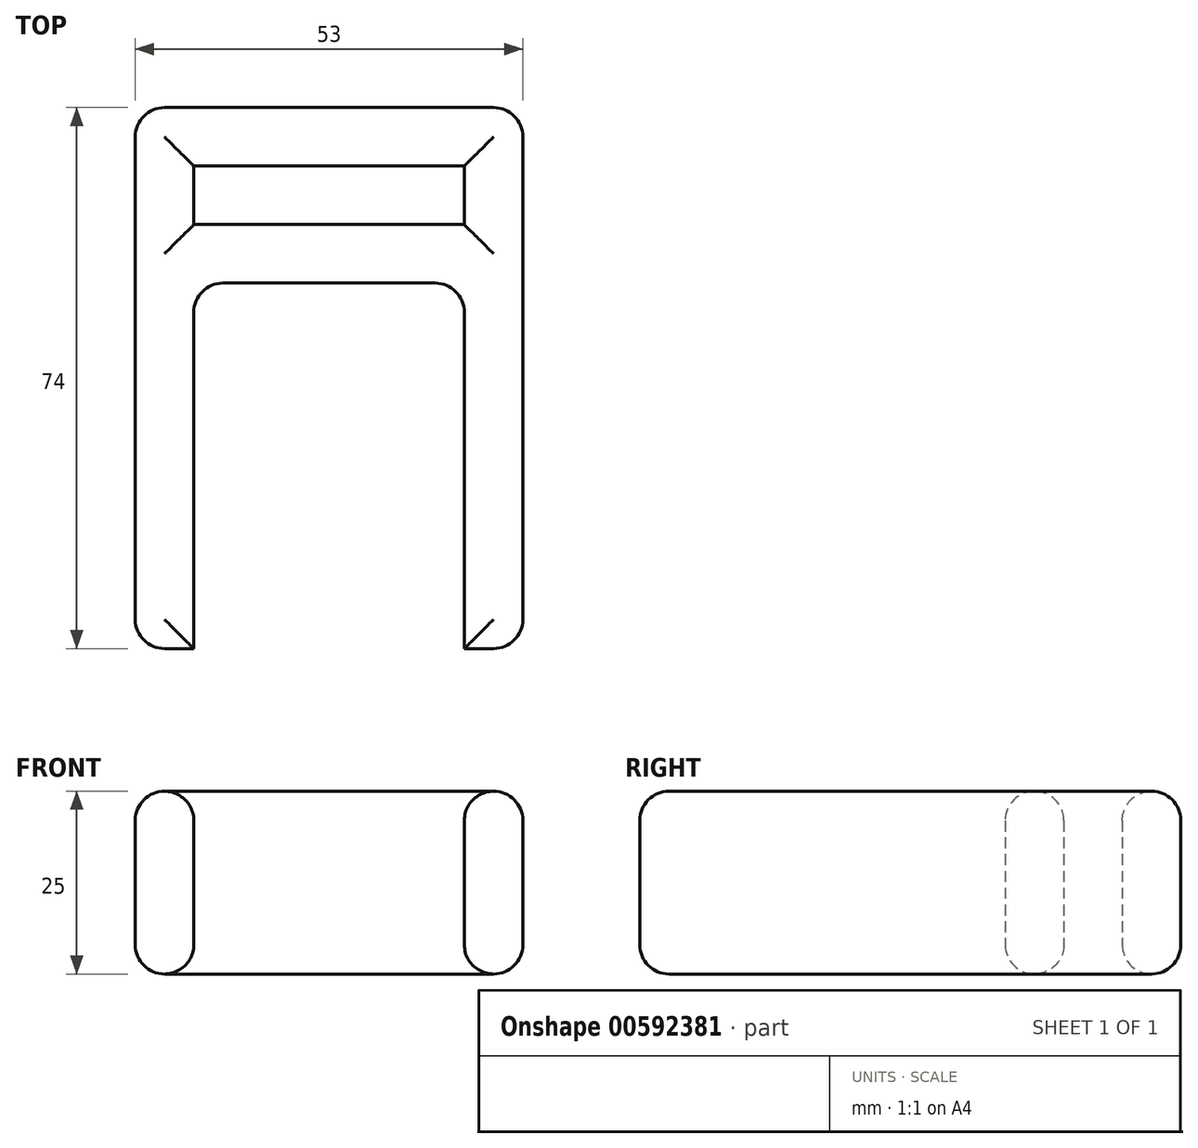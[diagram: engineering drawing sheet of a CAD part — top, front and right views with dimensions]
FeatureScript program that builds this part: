
annotation { "Feature Type Name" : "Feature", "Feature Type Description" : "" }
export const myFeature = defineFeature(function(context is Context, id is Id, definition is map)
    precondition{}
    {
        {
            var Q0;
            Q0=qCreatedBy(makeId("Top.planeOp"),FACE);
            var sketch = newSketch(context, id + "F0", { "sketchPlane" : qUnion([Q0])});
            skLineSegment(sketch, "E0.bottom", {"start": v(18.5, -25) * mm, "end": v(-18.5, -25) * mm});
            skLineSegment(sketch, "E0.top", {"start": v(18.5, 25) * mm, "end": v(-18.5, 25) * mm});
            skLineSegment(sketch, "E0.left", {"start": v(18.5, -25) * mm, "end": v(18.5, 25) * mm});
            skLineSegment(sketch, "E0.right", {"start": v(-18.5, -25) * mm, "end": v(-18.5, 25) * mm});
            skPoint(sketch, "E0.middle", {"position": v(0, 0) * mm});
            skLineSegment(sketch, "E1", {"start": v(-18.5, -25) * mm, "end": v(-26.5, -25) * mm});
            skLineSegment(sketch, "E2", {"start": v(18.5, -25) * mm, "end": v(26.5, -25) * mm});
            skLineSegment(sketch, "E3.bottom", {"start": v(-26.5, -25) * mm, "end": v(26.5, -25) * mm});
            skLineSegment(sketch, "E3.top", {"start": v(-26.5, 33) * mm, "end": v(26.5, 33) * mm});
            skLineSegment(sketch, "E3.left", {"start": v(-26.5, -25) * mm, "end": v(-26.5, 33) * mm});
            skLineSegment(sketch, "E3.right", {"start": v(26.5, -25) * mm, "end": v(26.5, 33) * mm});
            skLineSegment(sketch, "E4.top", {"start": v(-26.5, 49) * mm, "end": v(26.5, 49) * mm});
            skLineSegment(sketch, "E4.left", {"start": v(-26.5, 33) * mm, "end": v(-26.5, 49) * mm});
            skLineSegment(sketch, "E4.right", {"start": v(26.5, 33) * mm, "end": v(26.5, 49) * mm});
            skLineSegment(sketch, "E5.bottom", {"start": v(-18.5, 33) * mm, "end": v(18.5, 33) * mm});
            skLineSegment(sketch, "E5.top", {"start": v(-18.5, 41) * mm, "end": v(18.5, 41) * mm});
            skLineSegment(sketch, "E5.left", {"start": v(-18.5, 33) * mm, "end": v(-18.5, 41) * mm});
            skLineSegment(sketch, "E5.right", {"start": v(18.5, 33) * mm, "end": v(18.5, 41) * mm});
            skSolve(sketch);
        }
        {
            var Q0;
            Q0=makeQuery(id+"F0.imprint","IMPRINT",FACE,{"disambiguationData":[TD([[makeQuery(id+"F0.imprint","IMPRINT",EDGE,{"derivedFrom":sQuery(id+"F0.wireOp",EDGE,"E0.top")}),-1.0]])]});
            var Q1;
            Q1=makeQuery(id+"F0.imprint","IMPRINT",FACE,{"disambiguationData":[TD([[makeQuery(id+"F0.imprint","IMPRINT",EDGE,{"derivedFrom":sQuery(id+"F0.wireOp",EDGE,"E4.top")}),-1.0]])]});
            extrude(context, id + "F1", {"entities" : qUnion([Q0, Q1]), "depth" : 25 * mm, "offsetDistance" : 25 * mm});
        }
        {
            var Q0;
            Q0=makeQuery(id+"F1.opExtrude","SWEPT_EDGE",EDGE,{"disambiguationData":[OSD([sQuery(id+"F0.wireOp",EDGE,"E4.top"),sQuery(id+"F0.wireOp",EDGE,"E4.left")])]});
            var Q1;
            Q1=makeQuery(id+"F1.opExtrude","SWEPT_EDGE",EDGE,{"disambiguationData":[OSD([sQuery(id+"F0.wireOp",EDGE,"E4.top"),sQuery(id+"F0.wireOp",EDGE,"E4.right")])]});
            var Q2;
            Q2=makeQuery(id+"F1.opExtrude","SWEPT_EDGE",EDGE,{"disambiguationData":[OSD([sQuery(id+"F0.wireOp",EDGE,"E0.right"),sQuery(id+"F0.wireOp",EDGE,"E3.bottom")])]});
            var Q3;
            Q3=makeQuery(id+"F1.opExtrude","SWEPT_EDGE",EDGE,{"disambiguationData":[OSD([sQuery(id+"F0.wireOp",EDGE,"E0.left"),sQuery(id+"F0.wireOp",EDGE,"E3.bottom")])]});
            var Q4;
            Q4=makeQuery(id+"F1.opExtrude","SWEPT_EDGE",EDGE,{"disambiguationData":[OSD([sQuery(id+"F0.wireOp",EDGE,"E3.bottom"),sQuery(id+"F0.wireOp",EDGE,"E3.left")])]});
            var Q5;
            Q5=makeQuery(id+"F1.opExtrude","SWEPT_EDGE",EDGE,{"disambiguationData":[OSD([sQuery(id+"F0.wireOp",EDGE,"E3.bottom"),sQuery(id+"F0.wireOp",EDGE,"E3.right")])]});
            var Q6;
            Q6=makeQuery(id+"F1.opExtrude","CAP_EDGE",EDGE,{"disambiguationData":[OSD([sQuery(id+"F0.wireOp",EDGE,"E5.bottom")])],"isStart":false});
            var Q7;
            Q7=makeQuery(id+"F1.opExtrude","CAP_EDGE",EDGE,{"disambiguationData":[OSD([sQuery(id+"F0.wireOp",EDGE,"E5.left")])],"isStart":false});
            var Q8;
            Q8=makeQuery(id+"F1.opExtrude","CAP_EDGE",EDGE,{"disambiguationData":[OSD([sQuery(id+"F0.wireOp",EDGE,"E5.top")])],"isStart":false});
            var Q9;
            Q9=makeQuery(id+"F1.opExtrude","CAP_EDGE",EDGE,{"disambiguationData":[OSD([sQuery(id+"F0.wireOp",EDGE,"E5.right")])],"isStart":false});
            var Q10;
            Q10=makeQuery(id+"F1.opExtrude","CAP_EDGE",EDGE,{"disambiguationData":[OSD([sQuery(id+"F0.wireOp",EDGE,"E0.right")])],"isStart":false});
            var Q11;
            Q11=makeQuery(id+"F1.opExtrude","CAP_EDGE",EDGE,{"disambiguationData":[OSD([sQuery(id+"F0.wireOp",EDGE,"E0.top")])],"isStart":false});
            var Q12;
            Q12=makeQuery(id+"F1.opExtrude","SWEPT_FACE",FACE,{"disambiguationData":[OSD([sQuery(id+"F0.wireOp",EDGE,"E3.right"),sQuery(id+"F0.wireOp",EDGE,"E4.right")])]});
            var Q13;
            Q13=makeQuery(id+"F1.opExtrude","CAP_FACE",FACE,{"disambiguationData":[OSD([sQuery(id+"F0.wireOp",EDGE,"E0.top"),sQuery(id+"F0.wireOp",EDGE,"E0.left"),sQuery(id+"F0.wireOp",EDGE,"E0.right"),sQuery(id+"F0.wireOp",EDGE,"E3.bottom"),sQuery(id+"F0.wireOp",EDGE,"E3.left"),sQuery(id+"F0.wireOp",EDGE,"E3.right"),sQuery(id+"F0.wireOp",EDGE,"E4.top"),sQuery(id+"F0.wireOp",EDGE,"E4.left"),sQuery(id+"F0.wireOp",EDGE,"E4.right"),sQuery(id+"F0.wireOp",EDGE,"E5.bottom"),sQuery(id+"F0.wireOp",EDGE,"E5.top"),sQuery(id+"F0.wireOp",EDGE,"E5.left"),sQuery(id+"F0.wireOp",EDGE,"E5.right")])],"isStart":true});
            var Q14;
            Q14=makeQuery(id+"F1.opExtrude","CAP_FACE",FACE,{"disambiguationData":[OSD([sQuery(id+"F0.wireOp",EDGE,"E0.top"),sQuery(id+"F0.wireOp",EDGE,"E0.left"),sQuery(id+"F0.wireOp",EDGE,"E0.right"),sQuery(id+"F0.wireOp",EDGE,"E3.bottom"),sQuery(id+"F0.wireOp",EDGE,"E3.left"),sQuery(id+"F0.wireOp",EDGE,"E3.right"),sQuery(id+"F0.wireOp",EDGE,"E4.top"),sQuery(id+"F0.wireOp",EDGE,"E4.left"),sQuery(id+"F0.wireOp",EDGE,"E4.right"),sQuery(id+"F0.wireOp",EDGE,"E5.bottom"),sQuery(id+"F0.wireOp",EDGE,"E5.top"),sQuery(id+"F0.wireOp",EDGE,"E5.left"),sQuery(id+"F0.wireOp",EDGE,"E5.right")])],"isStart":false});
            fillet(context, id + "F2", {"entities" : qUnion([Q0, Q1, Q2, Q3, Q4, Q5, Q6, Q7, Q8, Q9, Q10, Q11, Q12, Q13, Q14]), "radius" : 4 * mm, "tangentPropagation" : true, "allowEdgeOverflow" : false});
        }
    });
